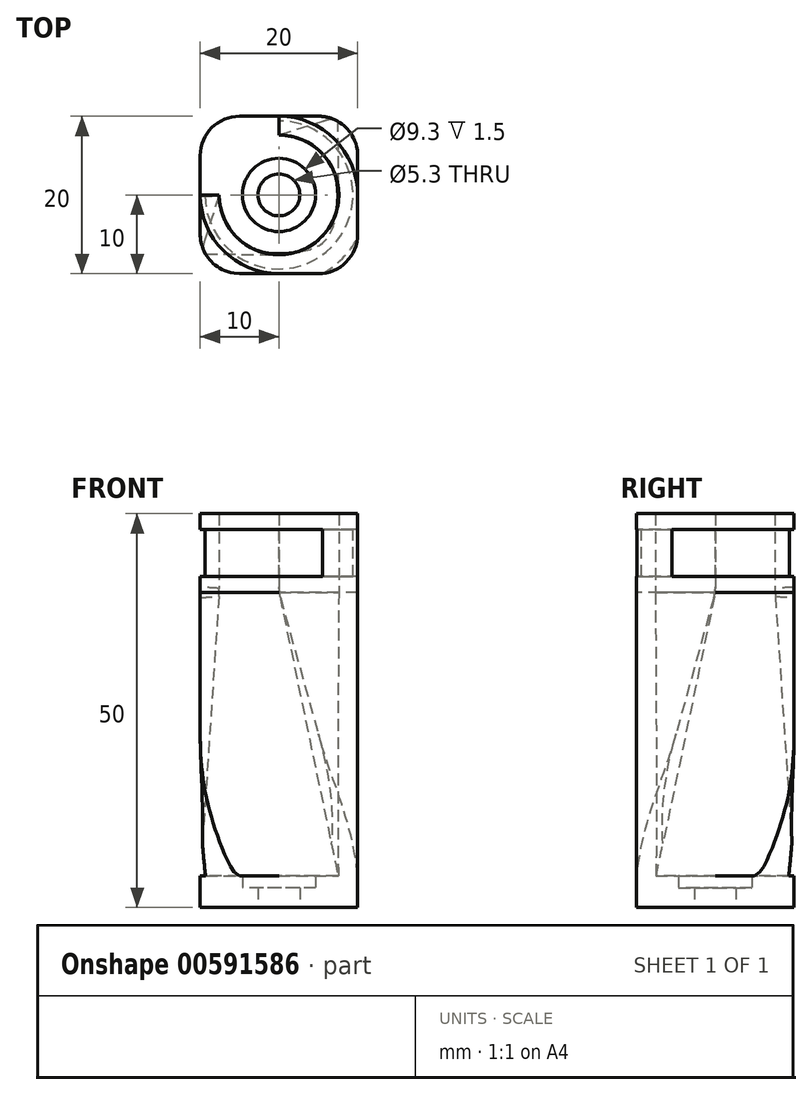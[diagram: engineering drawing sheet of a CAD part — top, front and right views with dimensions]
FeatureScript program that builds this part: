
annotation { "Feature Type Name" : "Feature", "Feature Type Description" : "" }
export const myFeature = defineFeature(function(context is Context, id is Id, definition is map)
    precondition{}
    {
        {
            var Q0;
            Q0=qCreatedBy(makeId("Top.planeOp"),FACE);
            var sketch = newSketch(context, id + "F0", { "sketchPlane" : qUnion([Q0])});
            skLineSegment(sketch, "E0.bottom", {"start": v(10, -10) * mm, "end": v(-10, -10) * mm});
            skLineSegment(sketch, "E0.top", {"start": v(10, 10) * mm, "end": v(-10, 10) * mm});
            skLineSegment(sketch, "E0.left", {"start": v(10, -10) * mm, "end": v(10, 10) * mm});
            skLineSegment(sketch, "E0.right", {"start": v(-10, -10) * mm, "end": v(-10, 10) * mm});
            skPoint(sketch, "E0.middle", {"position": v(0, 0) * mm});
            skCircle(sketch, "E1", {"center": v(0, 0) * mm, "radius": 2.65 * mm});
            skCircle(sketch, "E2", {"center": v(0, 0) * mm, "radius": 4.65 * mm});
            skSolve(sketch);
        }
        {
            var Q0;
            Q0=makeQuery(id+"F0.imprint","IMPRINT",FACE,{"disambiguationData":[TD([[makeQuery(id+"F0.imprint","IMPRINT",EDGE,{"derivedFrom":sQuery(id+"F0.wireOp",EDGE,"E0.bottom")}),-1.0]])]});
            extrude(context, id + "F1", {"entities" : qUnion([Q0]), "depth" : 4 * mm, "offsetDistance" : 25 * mm});
        }
        {
            var Q0;
            Q0=makeQuery(id+"F0.imprint","IMPRINT",FACE,{"disambiguationData":[TD([[makeQuery(id+"F0.imprint","IMPRINT",EDGE,{"derivedFrom":sQuery(id+"F0.wireOp",EDGE,"E1")}),-1.0]])]});
            extrude(context, id + "F2", {"entities" : qUnion([Q0]), "operationType" : NewBodyOperationType.ADD, "depth" : 2.5 * mm, "offsetDistance" : 25 * mm});
        }
        {
            var Q0;
            Q0=makeQuery(id+"F1.opExtrude","CAP_FACE",FACE,{"disambiguationData":[OSD([sQuery(id+"F0.wireOp",EDGE,"E0.bottom"),sQuery(id+"F0.wireOp",EDGE,"E0.top"),sQuery(id+"F0.wireOp",EDGE,"E0.left"),sQuery(id+"F0.wireOp",EDGE,"E0.right"),sQuery(id+"F0.wireOp",EDGE,"E2")])],"isStart":false});
            var sketch = newSketch(context, id + "F3", { "sketchPlane" : qUnion([Q0])});
            skFitSpline(sketch, "E3", {"points": [v(-10, -7.5) * mm, v(0, -7.5) * mm, v(5.84, -5.84) * mm, v(7.5, 0) * mm, v(7.5, 10) * mm], "startDerivative": vector(37.36, 0) * mm, "endDerivative": vector(0, 37.36) * mm});
            skLineSegment(sketch, "E4", {"start": v(0, 0) * mm, "end": v(10, -10) * mm, "construction": true});
            skSolve(sketch);
        }
        {
            var Q0;
            {var subQ2=sQuery(id+"F3.wireOp",EDGE,"E3");Q0=makeQuery(id+"F3.imprint","IMPRINT",FACE,{"disambiguationData":[TD([[makeQuery(id+"F3.imprint","IMPRINT",EDGE,{"derivedFrom":subQ2}),-1.0]])]});}
            cPlane(context, id + "F4", {"entities" : qUnion([Q0]), "cplaneType" : CPlaneType.OFFSET, "offset" : 36 * mm, "width" : 150 * mm, "height" : 150 * mm});
        }
        {
            var Q0;
            Q0=qCreatedBy(id+"F4.planeOp",FACE);
            var sketch = newSketch(context, id + "F5", { "sketchPlane" : qUnion([Q0])});
            skArc(sketch, "E5", {"start": v(-7.6, 0) * mm, "mid": v(5.37, -5.37) * mm, "end": v(0, 7.6) * mm});
            skArc(sketch, "E6", {"start": v(-10, 0) * mm, "mid": v(-7.07, -7.07) * mm, "end": v(0, -10) * mm});
            skLineSegment(sketch, "E7", {"start": v(-10, 0) * mm, "end": v(-7.6, 0) * mm});
            skLineSegment(sketch, "E8", {"start": v(0, 7.6) * mm, "end": v(0, 10) * mm});
            skLineSegment(sketch, "E9", {"start": v(0, -10) * mm, "end": v(10, -10) * mm});
            skLineSegment(sketch, "E10", {"start": v(10, -10) * mm, "end": v(10, 0) * mm});
            skLineSegment(sketch, "E11", {"start": v(0, -10) * mm, "end": v(0, -7.6) * mm});
            skLineSegment(sketch, "E12", {"start": v(7.6, 0) * mm, "end": v(10, 0) * mm});
            skArc(sketch, "E13.trimOffspring", {"start": v(10, 0) * mm, "mid": v(7.07, 7.07) * mm, "end": v(0, 10) * mm});
            skSolve(sketch);
        }
        {
            var Q0;
            Q0=makeQuery(id+"F5.imprint","IMPRINT",FACE,{"disambiguationData":[TD([[makeQuery(id+"F5.imprint","IMPRINT",EDGE,{"derivedFrom":sQuery(id+"F5.wireOp",EDGE,"E5")}),-1.0]])]});
            var Q1;
            {var subQ0=sQuery(id+"F5.wireOp",EDGE,"E9");Q1=makeQuery(id+"F5.imprint","IMPRINT",FACE,{"disambiguationData":[TD([[makeQuery(id+"F5.imprint","IMPRINT",EDGE,{"derivedFrom":subQ0}),1.0]])]});}
            extrude(context, id + "F6", {"entities" : qUnion([Q0, Q1]), "depth" : 10 * mm, "offsetDistance" : 25 * mm});
        }
        {
            var Q0;
            Q0=makeQuery(id+"F5.imprint","IMPRINT",FACE,{"disambiguationData":[TD([[makeQuery(id+"F5.imprint","IMPRINT",EDGE,{"derivedFrom":sQuery(id+"F5.wireOp",EDGE,"E9")}),1.0]])]});
            var Q1;
            {var subQ2=sQuery(id+"F3.wireOp",EDGE,"E3");Q1=makeQuery(id+"F3.imprint","IMPRINT",FACE,{"disambiguationData":[TD([[makeQuery(id+"F3.imprint","IMPRINT",EDGE,{"derivedFrom":subQ2}),-1.0]])]});}
            loft(context, id + "F7", {"sheetProfilesArray" : [{ "sheetProfileEntities" : qUnion([Q0]) }, { "sheetProfileEntities" : qUnion([Q1]) }]});
        }
        {
            var Q0;
            Q0=makeQuery(id+"F1.opExtrude","SWEPT_BODY",BODY,{"disambiguationData":[OSD([sQuery(id+"F0.wireOp",EDGE,"E0.bottom"),sQuery(id+"F0.wireOp",EDGE,"E0.top"),sQuery(id+"F0.wireOp",EDGE,"E0.left"),sQuery(id+"F0.wireOp",EDGE,"E0.right"),sQuery(id+"F0.wireOp",EDGE,"E2")])]});
            var Q1;
            Q1=makeQuery(id+"F6.opExtrude","SWEPT_BODY",BODY,{"disambiguationData":[OSD([sQuery(id+"F5.wireOp",EDGE,"E5"),sQuery(id+"F5.wireOp",EDGE,"E6"),sQuery(id+"F5.wireOp",EDGE,"E7"),sQuery(id+"F5.wireOp",EDGE,"E8"),sQuery(id+"F5.wireOp",EDGE,"E9"),sQuery(id+"F5.wireOp",EDGE,"E10"),sQuery(id+"F5.wireOp",EDGE,"E13.trimOffspring")])]});
            var Q2;
            {var subQ5=sQuery(id+"F3.wireOp",EDGE,"E3");Q2=makeQuery(id+"F7.opLoft","SWEPT_BODY",BODY,{"disambiguationData":[OSD([makeQuery(id+"F3.imprint","IMPRINT",FACE,{"disambiguationData":[TD([[makeQuery(id+"F3.imprint","IMPRINT",EDGE,{"derivedFrom":subQ5}),-1.0]])]}),makeQuery(id+"F5.imprint","IMPRINT",FACE,{"disambiguationData":[TD([[makeQuery(id+"F5.imprint","IMPRINT",EDGE,{"derivedFrom":sQuery(id+"F5.wireOp",EDGE,"E9")}),1.0]])]})])]});}
            booleanBodies(context, id + "F8", {"operationType" : BooleanOperationType.UNION, "tools" : qUnion([Q0, Q1, Q2])});
        }
        {
            var Q0;
            Q0=makeQuery(id+"F1.opExtrude","SWEPT_EDGE",EDGE,{"disambiguationData":[OSD([sQuery(id+"F0.wireOp",EDGE,"E0.top"),sQuery(id+"F0.wireOp",EDGE,"E0.right")])]});
            var Q1;
            Q1=makeQuery(id+"F1.opExtrude","SWEPT_EDGE",EDGE,{"disambiguationData":[OSD([sQuery(id+"F0.wireOp",EDGE,"E0.top"),sQuery(id+"F0.wireOp",EDGE,"E0.left")])]});
            var Q2;
            Q2=makeQuery(id+"F1.opExtrude","SWEPT_EDGE",EDGE,{"disambiguationData":[OSD([sQuery(id+"F0.wireOp",EDGE,"E0.bottom"),sQuery(id+"F0.wireOp",EDGE,"E0.right")])]});
            fillet(context, id + "F9", {"entities" : qUnion([Q0, Q1, Q2]), "radius" : 5 * mm, "tangentPropagation" : true, "allowEdgeOverflow" : false});
        }
        {
            var Q0;
            {var subQ0=sQuery(id+"F5.wireOp",EDGE,"E10");var subQ1=sQuery(id+"F5.wireOp",EDGE,"E9");var subQ2=sQuery(id+"F0.wireOp",EDGE,"E0.left");var subQ3=sQuery(id+"F0.wireOp",EDGE,"E0.bottom");Q0=makeQuery(id+"F8.opBoolean","MERGE",EDGE,{"derivedFrom":[makeQuery(id+"F1.opExtrude","SWEPT_EDGE",EDGE,{"disambiguationData":[OSD([subQ3,subQ2])]}),makeQuery(id+"F6.opExtrude","SWEPT_EDGE",EDGE,{"disambiguationData":[OSD([subQ1,subQ0])]}),makeQuery(id+"F7.opLoft","SWEPT_EDGE",EDGE,{"disambiguationData":[OSD([subQ3,subQ2,subQ1,subQ0])]})]});}
            fillet(context, id + "F10", {"entities" : qUnion([Q0]), "radius" : 5 * mm, "tangentPropagation" : true, "allowEdgeOverflow" : false});
        }
        {
            var Q0;
            Q0=makeQuery(id+"F6.opExtrude","CAP_FACE",FACE,{"disambiguationData":[OSD([sQuery(id+"F5.wireOp",EDGE,"E5"),sQuery(id+"F5.wireOp",EDGE,"E6"),sQuery(id+"F5.wireOp",EDGE,"E7"),sQuery(id+"F5.wireOp",EDGE,"E8"),sQuery(id+"F5.wireOp",EDGE,"E9"),sQuery(id+"F5.wireOp",EDGE,"E10"),sQuery(id+"F5.wireOp",EDGE,"E13.trimOffspring")])],"isStart":false});
            var sketch = newSketch(context, id + "F11", { "sketchPlane" : qUnion([Q0])});
            skCircle(sketch, "E14", {"center": v(0, 0) * mm, "radius": 9.4 * mm});
            skCircle(sketch, "E15", {"center": v(0, 0) * mm, "radius": 11.4 * mm});
            skSolve(sketch);
        }
        {
            var Q0;
            Q0 = qSketchRegion(id + "F11", true);
            extrude(context, id + "F12", {"entities" : qUnion([Q0]), "operationType" : NewBodyOperationType.REMOVE, "oppositeDirection" : true, "depth" : 8 * mm, "offsetDistance" : 25 * mm, "hasSecondDirection" : true, "secondDirectionOppositeDirection" : true, "secondDirectionDepth" : 2 * mm});
        }
        {
            var Q0;
            Q0=makeQuery(id+"F7.opLoft","MID_CAP_EDGE",EDGE,{"disambiguationData":[OSD([sQuery(id+"F5.wireOp",EDGE,"E5"),sQuery(id+"F5.wireOp",EDGE,"E10"),sQuery(id+"F5.wireOp",EDGE,"E12"),sQuery(id+"F5.wireOp",EDGE,"E13.trimOffspring")])],"capPos":0.0});
            var Q1;
            Q1=makeQuery(id+"F7.opLoft","MID_CAP_EDGE",EDGE,{"disambiguationData":[OSD([sQuery(id+"F5.wireOp",EDGE,"E5"),sQuery(id+"F5.wireOp",EDGE,"E6"),sQuery(id+"F5.wireOp",EDGE,"E9"),sQuery(id+"F5.wireOp",EDGE,"E11")])],"capPos":0.0});
            chamfer(context, id + "F13", {"entities" : qUnion([Q0, Q1]), "width" : 5 * mm, "tangentPropagation" : true});
        }
    });
